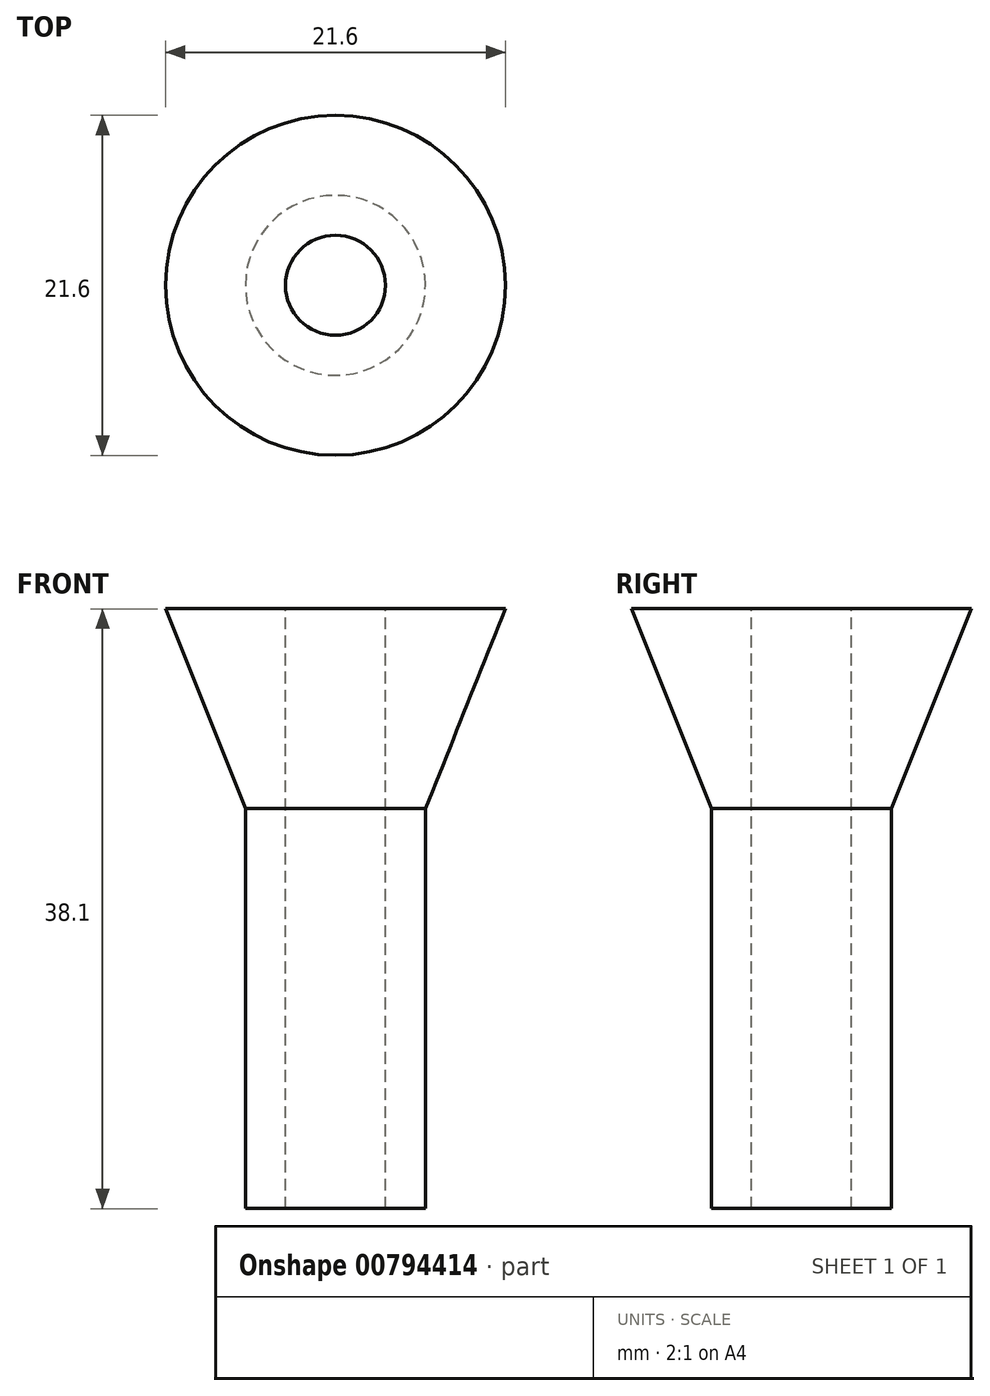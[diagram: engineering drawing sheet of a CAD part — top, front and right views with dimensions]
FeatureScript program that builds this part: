
annotation { "Feature Type Name" : "Feature", "Feature Type Description" : "" }
export const myFeature = defineFeature(function(context is Context, id is Id, definition is map)
    precondition{}
    {
        {
            var Q0;
            Q0=qCreatedBy(makeId("Front.planeOp"),FACE);
            var sketch = newSketch(context, id + "F0", { "sketchPlane" : qUnion([Q0])});
            skLineSegment(sketch, "E0", {"start": v(0, 42.58) * mm, "end": v(0, 29.88) * mm});
            skLineSegment(sketch, "E1", {"start": v(0, 29.88) * mm, "end": v(5.72, 29.88) * mm});
            skLineSegment(sketch, "E2", {"start": v(0, 42.58) * mm, "end": v(10.8, 42.58) * mm});
            skLineSegment(sketch, "E3", {"start": v(10.8, 42.58) * mm, "end": v(5.72, 29.88) * mm});
            skSolve(sketch);
        }
        {
            var Q0;
            Q0 = qSketchRegion(id + "F0", true);
            var Q1;
            Q1=sQuery(id+"F0.wireOp",EDGE,"E0");
            revolve(context, id + "F1", {"surfaceOperationType" : NewSurfaceOperationType.NEW, "entities" : qUnion([Q0]), "axis" : qUnion([Q1]), "revolveType" : RevolveType.FULL});
        }
        {
            var Q0;
            Q0=makeQuery(id+"F1.opRevolve","SWEPT_FACE",FACE,{"disambiguationData":[OSD([sQuery(id+"F0.wireOp",EDGE,"E1")])]});
            var sketch = newSketch(context, id + "F2", { "sketchPlane" : qUnion([Q0])});
            skCircle(sketch, "E4", {"center": v(0, 0) * mm, "radius": 5.72 * mm});
            skSolve(sketch);
        }
        {
            var Q0;
            Q0 = qSketchRegion(id + "F2", true);
            extrude(context, id + "F3", {"entities" : qUnion([Q0]), "operationType" : NewBodyOperationType.ADD, "depth" : 25.4 * mm, "offsetDistance" : 25.4 * mm});
        }
        {
            var Q0;
            Q0=makeQuery(id+"F1.opRevolve","SWEPT_FACE",FACE,{"disambiguationData":[OSD([sQuery(id+"F0.wireOp",EDGE,"E2")])]});
            var sketch = newSketch(context, id + "F4", { "sketchPlane" : qUnion([Q0])});
            skCircle(sketch, "E5", {"center": v(0, 0) * mm, "radius": 3.18 * mm});
            skSolve(sketch);
        }
        {
            var Q0;
            Q0 = qSketchRegion(id + "F4", true);
            extrude(context, id + "F5", {"entities" : qUnion([Q0]), "operationType" : NewBodyOperationType.REMOVE, "oppositeDirection" : true, "depth" : 38.1 * mm, "offsetDistance" : 25.4 * mm});
        }
    });
